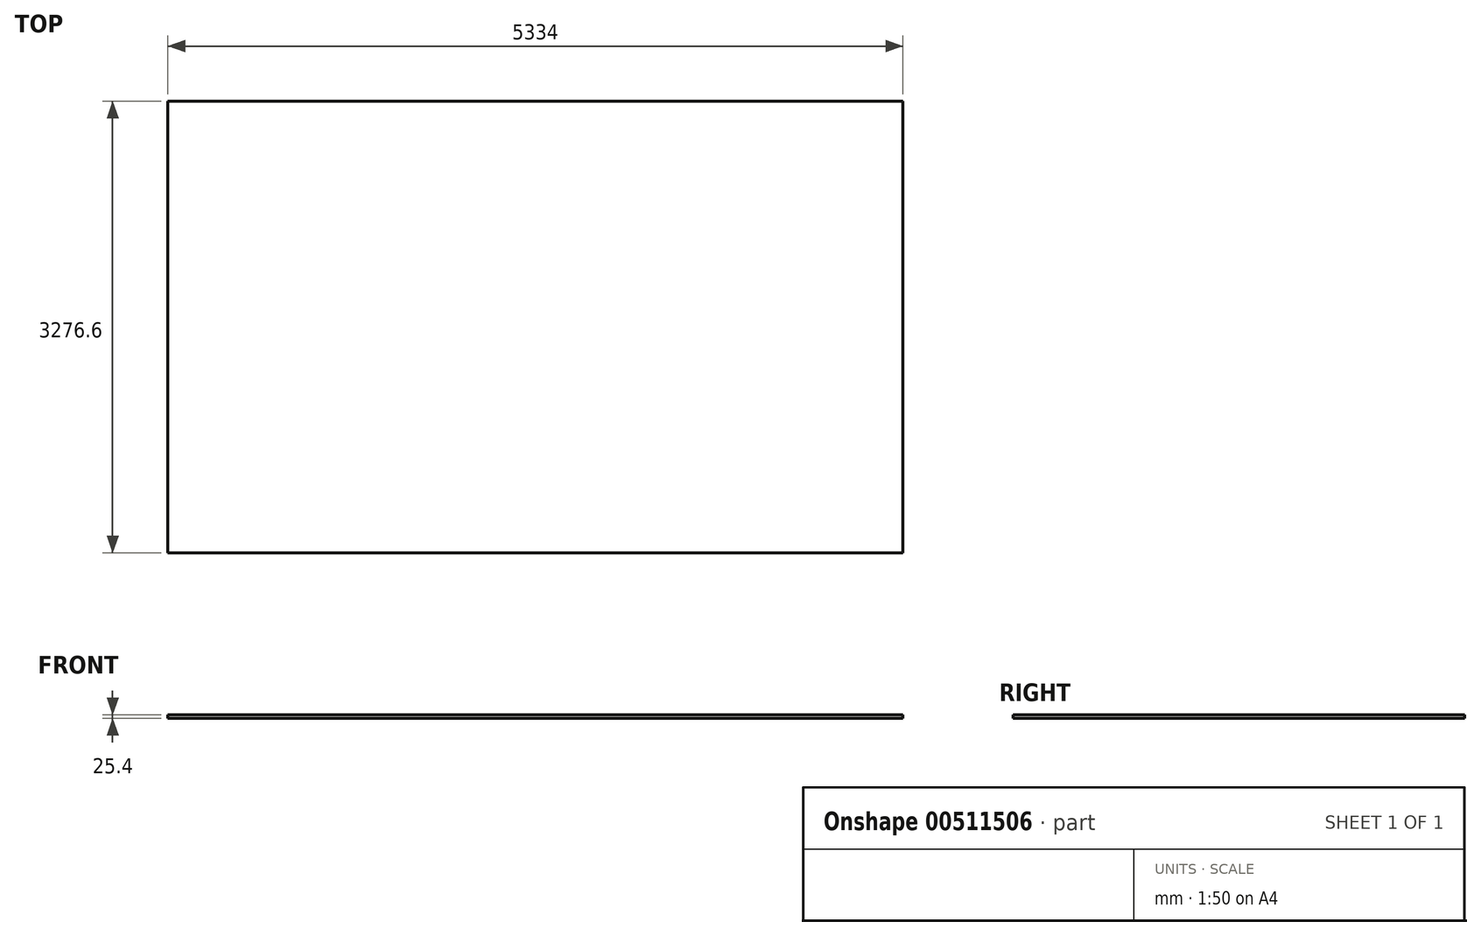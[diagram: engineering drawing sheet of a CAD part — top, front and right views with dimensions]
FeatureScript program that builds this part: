
annotation { "Feature Type Name" : "Feature", "Feature Type Description" : "" }
export const myFeature = defineFeature(function(context is Context, id is Id, definition is map)
    precondition{}
    {
        {
            var Q0;
            Q0=qCreatedBy(makeId("Top.planeOp"),FACE);
            var sketch = newSketch(context, id + "F0", { "sketchPlane" : qUnion([Q0])});
            skLineSegment(sketch, "E0.bottom", {"start": v(0, 0) * mm, "end": v(5334, 0) * mm});
            skLineSegment(sketch, "E0.top", {"start": v(0, 3276.6) * mm, "end": v(5334, 3276.6) * mm});
            skLineSegment(sketch, "E0.left", {"start": v(0, 0) * mm, "end": v(0, 3276.6) * mm});
            skLineSegment(sketch, "E0.right", {"start": v(5334, 0) * mm, "end": v(5334, 3276.6) * mm});
            skSolve(sketch);
        }
        {
            var Q0;
            Q0=makeQuery(id+"F0.imprint","IMPRINT",FACE,{"disambiguationData":[TD([[makeQuery(id+"F0.imprint","IMPRINT",EDGE,{"derivedFrom":sQuery(id+"F0.wireOp",EDGE,"E0.bottom")}),1.0]])]});
            extrude(context, id + "F1", {"entities" : qUnion([Q0]), "depth" : 25.4 * mm});
        }
    });
